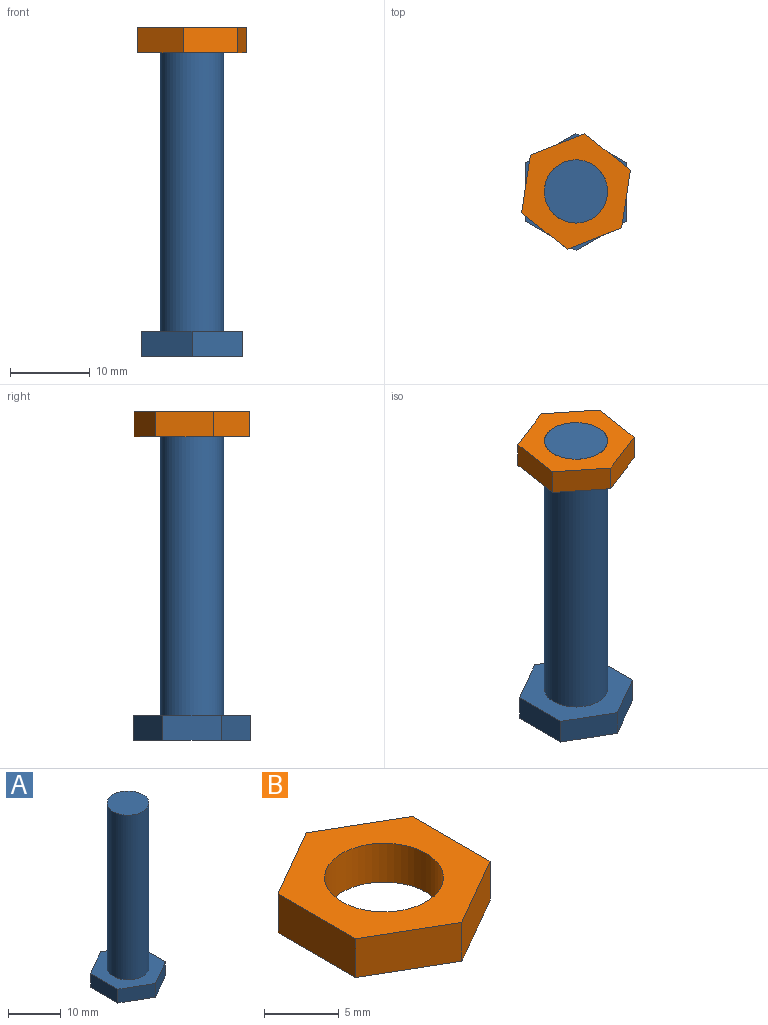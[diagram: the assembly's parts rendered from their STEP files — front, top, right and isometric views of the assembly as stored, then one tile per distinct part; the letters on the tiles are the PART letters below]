
ASSEMBLY  parts=2 mates=1
PART A: 10 faces, bbox 12.7x14.7x41.3 mm
  f0: cylinder r=3.97mm len=38.1mm, axis (0,0,-1), area 950.1mm2, adj f1,f9
  f1: plane 7.94x7.94mm, normal (0,0,1), area 49.5mm2, adj f0
  f2: plane 7.33x3.18mm, normal (1,0,0), area 23.3mm2, adj f3,f7,f8,f9
  f3: plane 6.35x3.67mm, normal (0.5,0.87,0), area 23.3mm2, adj f2,f4,f8,f9
  f4: plane 6.35x3.67mm, normal (-0.5,0.87,0), area 23.3mm2, adj f3,f5,f8,f9
  f5: plane 7.33x3.18mm, normal (-1,0,0), area 23.3mm2, adj f4,f6,f8,f9
  f6: plane 6.35x3.67mm, normal (-0.5,-0.87,0), area 23.3mm2, adj f5,f7,f8,f9
  f7: plane 6.35x3.67mm, normal (0.5,-0.87,0), area 23.3mm2, adj f2,f6,f8,f9
  f8: plane 14.66x12.7mm, normal (0,0,-1), area 139.7mm2, adj f2,f3,f4,f5,f6,f7
  f9: plane 14.66x12.7mm, normal (0,0,1), area 90.2mm2, adj f0,f2,f3,f4,f5,f6,f7
PART B: 9 faces, bbox 12.7x14.7x3.2 mm
  f0: plane 7.33x3.18mm, normal (1,0,0), area 23.3mm2, adj f1,f5,f7,f8
  f1: plane 6.35x3.67mm, normal (0.5,0.87,0), area 23.3mm2, adj f0,f2,f7,f8
  f2: plane 6.35x3.67mm, normal (-0.5,0.87,0), area 23.3mm2, adj f1,f3,f7,f8
  f3: plane 7.33x3.18mm, normal (-1,0,0), area 23.3mm2, adj f2,f4,f7,f8
  f4: plane 6.35x3.67mm, normal (-0.5,-0.87,0), area 23.3mm2, adj f3,f5,f7,f8
  f5: plane 6.35x3.67mm, normal (0.5,-0.87,0), area 23.3mm2, adj f0,f4,f7,f8
  f6: cylinder r=3.97mm len=7.94mm, axis (0,0,-1), area 79.2mm2, adj f7,f8
  f7: plane 14.66x12.7mm, normal (0,0,1), area 90.2mm2, adj f0,f1,f2,f3,f4,f5,f6
  f8: plane 14.66x12.7mm, normal (0,0,-1), area 90.2mm2, adj f0,f1,f2,f3,f4,f5,f6
PLACE A t=(-6.78,-3.01,-0.23)mm fixed
PLACE B rot(axis=(0,0,1),51.5deg) t=(-6.78,-3.01,34.69)mm
MATE revolute B.f6 <-> A.f0  axis (0,0,1) through (-6.78,-3.01,37.87)mm
